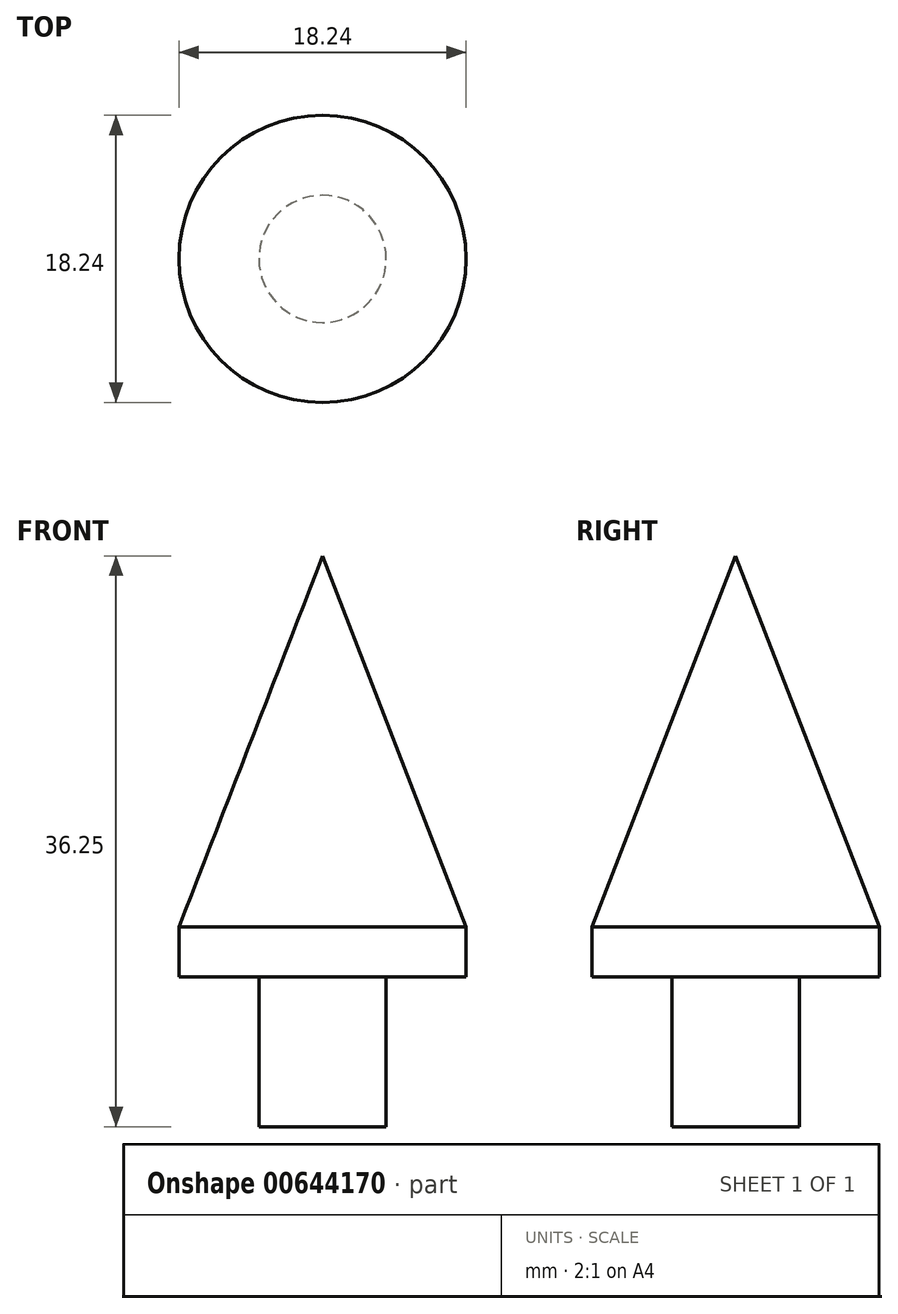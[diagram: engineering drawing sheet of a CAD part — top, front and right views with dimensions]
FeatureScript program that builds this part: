
annotation { "Feature Type Name" : "Feature", "Feature Type Description" : "" }
export const myFeature = defineFeature(function(context is Context, id is Id, definition is map)
    precondition{}
    {
        {
            var Q0;
            Q0=qCreatedBy(makeId("Front.planeOp"),FACE);
            var sketch = newSketch(context, id + "F0", { "sketchPlane" : qUnion([Q0])});
            skLineSegment(sketch, "E0", {"start": v(0, 0) * mm, "end": v(0, -9.5) * mm});
            skLineSegment(sketch, "E1", {"start": v(0, -9.5) * mm, "end": v(-4.04, -9.5) * mm});
            skLineSegment(sketch, "E2", {"start": v(-4.04, -9.5) * mm, "end": v(-4.04, 0) * mm});
            skLineSegment(sketch, "E3", {"start": v(-4.04, 0) * mm, "end": v(-9.12, 0) * mm});
            skLineSegment(sketch, "E4", {"start": v(-9.12, 0) * mm, "end": v(-9.12, 3.18) * mm});
            skLineSegment(sketch, "E5", {"start": v(0, 0) * mm, "end": v(0, 3.18) * mm});
            skLineSegment(sketch, "E6", {"start": v(0, 3.18) * mm, "end": v(0, 26.75) * mm});
            skLineSegment(sketch, "E7", {"start": v(0, 26.75) * mm, "end": v(-9.12, 3.18) * mm});
            skSolve(sketch);
        }
        {
            var Q0;
            Q0 = qSketchRegion(id + "F0", true);
            var Q1;
            Q1=sQuery(id+"F0.wireOp",EDGE,"E6");
            revolve(context, id + "F1", {"entities" : qUnion([Q0]), "axis" : qUnion([Q1]), "revolveType" : RevolveType.FULL});
        }
    });
